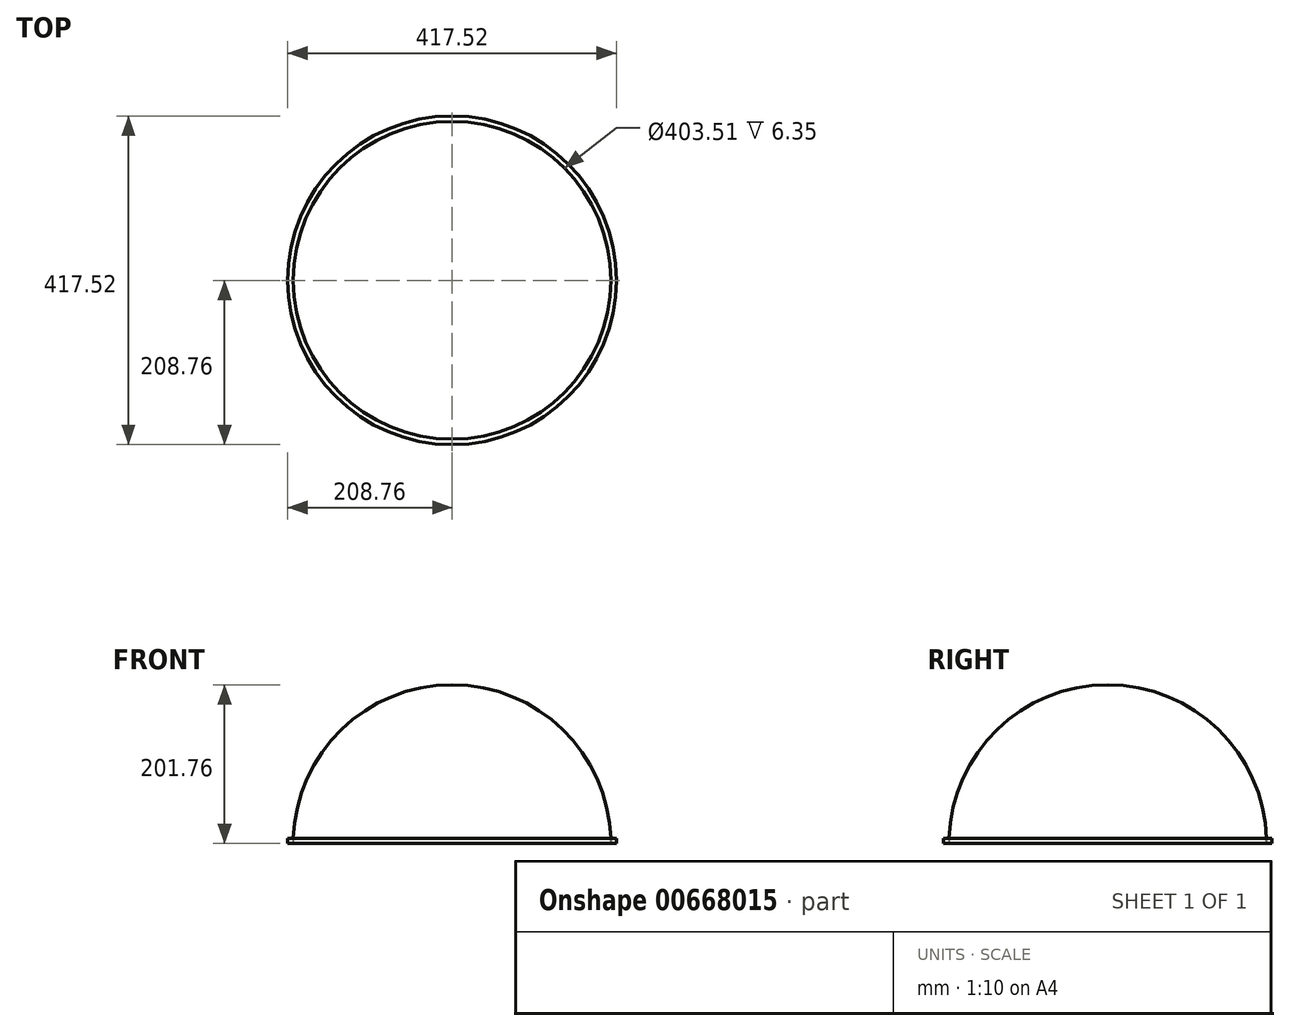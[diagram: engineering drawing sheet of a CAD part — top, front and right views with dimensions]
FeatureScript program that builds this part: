
annotation { "Feature Type Name" : "Feature", "Feature Type Description" : "" }
export const myFeature = defineFeature(function(context is Context, id is Id, definition is map)
    precondition{}
    {
        {
            var Q0;
            Q0=qCreatedBy(makeId("Top.planeOp"),FACE);
            var sketch = newSketch(context, id + "F0", { "sketchPlane" : qUnion([Q0])});
            skArc(sketch, "E0", {"start": v(0, -208.76) * mm, "mid": v(208.76, 0) * mm, "end": v(0, 208.76) * mm});
            skArc(sketch, "E1", {"start": v(0, -201.76) * mm, "mid": v(201.76, 0) * mm, "end": v(0, 201.76) * mm});
            skLineSegment(sketch, "E2", {"start": v(0, 208.76) * mm, "end": v(0, -208.76) * mm});
            skArc(sketch, "E3", {"start": v(0, 201.76) * mm, "mid": v(-201.76, 0) * mm, "end": v(0, -201.76) * mm});
            skArc(sketch, "E4", {"start": v(0, 208.76) * mm, "mid": v(-208.76, 0) * mm, "end": v(0, -208.76) * mm});
            skSolve(sketch);
        }
        {
            var Q0;
            {var subQ0=sQuery(id+"F0.wireOp",EDGE,"E1");Q0=makeQuery(id+"F0.imprint","IMPRINT",FACE,{"disambiguationData":[TD([[makeQuery(id+"F0.imprint","IMPRINT",EDGE,{"derivedFrom":subQ0}),1.0]])]});}
            var Q1;
            Q1=sQuery(id+"F0.wireOp",EDGE,"E2");
            revolve(context, id + "F1", {"entities" : qUnion([Q0]), "axis" : qUnion([Q1]), "revolveType" : RevolveType.ONE_DIRECTION, "angle" : 180 * degree});
        }
        {
            var Q0;
            {var subQ0=sQuery(id+"F0.wireOp",EDGE,"E0");Q0=makeQuery(id+"F0.imprint","IMPRINT",FACE,{"disambiguationData":[TD([[makeQuery(id+"F0.imprint","IMPRINT",EDGE,{"derivedFrom":subQ0}),1.0]])]});}
            var Q1;
            {var subQ3=sQuery(id+"F0.wireOp",EDGE,"E3");Q1=makeQuery(id+"F0.imprint","IMPRINT",FACE,{"disambiguationData":[TD([[makeQuery(id+"F0.imprint","IMPRINT",EDGE,{"derivedFrom":subQ3}),-1.0]])]});}
            extrude(context, id + "F2", {"entities" : qUnion([Q0, Q1]), "depth" : 6.35 * mm, "offsetDistance" : 25.4 * mm});
        }
    });
